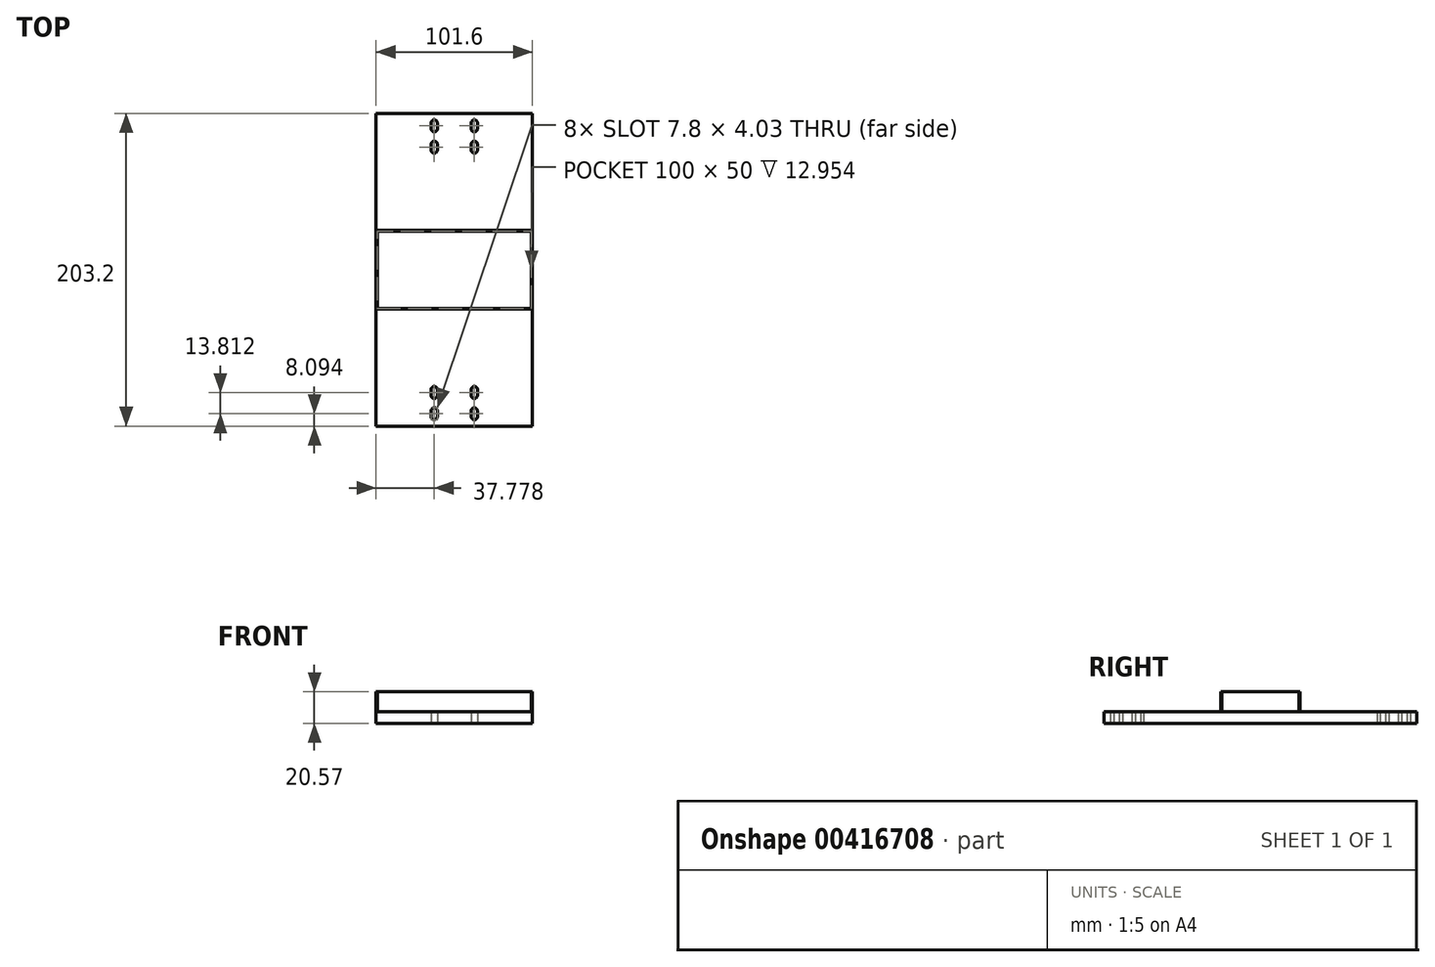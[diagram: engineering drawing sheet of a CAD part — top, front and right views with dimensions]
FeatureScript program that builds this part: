
annotation { "Feature Type Name" : "Feature", "Feature Type Description" : "" }
export const myFeature = defineFeature(function(context is Context, id is Id, definition is map)
    precondition{}
    {
        {
            var Q0;
            Q0=qCreatedBy(makeId("Top.planeOp"),FACE);
            var sketch = newSketch(context, id + "F0", { "sketchPlane" : qUnion([Q0])});
            skLineSegment(sketch, "E0.bottom", {"start": v(-50.8, 101.6) * mm, "end": v(50.8, 101.6) * mm});
            skLineSegment(sketch, "E0.top", {"start": v(-50.8, -101.6) * mm, "end": v(50.8, -101.6) * mm});
            skLineSegment(sketch, "E0.left", {"start": v(-50.8, 101.6) * mm, "end": v(-50.8, -101.6) * mm});
            skLineSegment(sketch, "E0.right", {"start": v(50.8, 101.6) * mm, "end": v(50.8, -101.6) * mm});
            skPoint(sketch, "E0.middle", {"position": v(0, 0) * mm});
            skSolve(sketch);
        }
        {
            var Q0;
            Q0=qSketchRegion(id+"F0",true);
            extrude(context, id + "F1", {"entities" : qUnion([Q0]), "depth" : 7.62 * mm});
        }
        {
            var Q0;
            Q0=qCreatedBy(makeId("Top.planeOp"),FACE);
            var sketch = newSketch(context, id + "F2", { "sketchPlane" : qUnion([Q0])});
            skLineSegment(sketch, "E1.top", {"start": v(-19, -101.6) * mm, "end": v(19, -101.6) * mm});
            skArc(sketch, "E2", {"start": v(-14.99, -81.42) * mm, "mid": v(-13.08, -83.6) * mm, "end": v(-11, -81.58) * mm});
            skArc(sketch, "E3", {"start": v(-11.05, -77.84) * mm, "mid": v(-13.03, -75.8) * mm, "end": v(-15.04, -77.82) * mm});
            skLineSegment(sketch, "E4", {"start": v(-11.05, -77.84) * mm, "end": v(-11, -81.58) * mm});
            skLineSegment(sketch, "E5", {"start": v(-15.04, -77.82) * mm, "end": v(-14.99, -81.42) * mm});
            skLineSegment(sketch, "E6.MirrorCS", {"start": v(-11.05, -95.36) * mm, "end": v(-11, -91.62) * mm});
            skLineSegment(sketch, "E7.MirrorCS", {"start": v(-15.04, -95.38) * mm, "end": v(-14.99, -91.78) * mm});
            skArc(sketch, "E8.MirrorCS", {"start": v(-14.99, -91.78) * mm, "mid": v(-13.08, -89.6) * mm, "end": v(-11, -91.62) * mm});
            skArc(sketch, "E9.MirrorCS", {"start": v(-11.05, -95.36) * mm, "mid": v(-13.03, -97.4) * mm, "end": v(-15.04, -95.38) * mm});
            skLineSegment(sketch, "E10.MirrorCS", {"start": v(11.05, -77.84) * mm, "end": v(11, -81.58) * mm});
            skLineSegment(sketch, "E11.MirrorCS", {"start": v(15.04, -77.82) * mm, "end": v(14.99, -81.42) * mm});
            skArc(sketch, "E12.MirrorCS", {"start": v(14.99, -81.42) * mm, "mid": v(13.08, -83.6) * mm, "end": v(11, -81.58) * mm});
            skArc(sketch, "E13.MirrorCS", {"start": v(11.05, -77.84) * mm, "mid": v(13.03, -75.8) * mm, "end": v(15.04, -77.82) * mm});
            skArc(sketch, "E14.MirrorCS", {"start": v(11.05, -95.36) * mm, "mid": v(13.03, -97.4) * mm, "end": v(15.04, -95.38) * mm});
            skLineSegment(sketch, "E15.MirrorCS", {"start": v(11.05, -95.36) * mm, "end": v(11, -91.62) * mm});
            skArc(sketch, "E16.MirrorCS", {"start": v(14.99, -91.78) * mm, "mid": v(13.08, -89.6) * mm, "end": v(11, -91.62) * mm});
            skLineSegment(sketch, "E17", {"start": v(14.99, -91.78) * mm, "end": v(15.04, -95.38) * mm});
            skLineSegment(sketch, "E18.MirrorCS", {"start": v(11.05, 95.36) * mm, "end": v(11, 91.62) * mm});
            skArc(sketch, "E19.MirrorCS", {"start": v(-11.05, 95.36) * mm, "mid": v(-13.03, 97.4) * mm, "end": v(-15.04, 95.38) * mm});
            skLineSegment(sketch, "E20.MirrorCS", {"start": v(-11.05, 77.84) * mm, "end": v(-11, 81.58) * mm});
            skLineSegment(sketch, "E21.MirrorCS", {"start": v(15.04, 77.82) * mm, "end": v(14.99, 81.42) * mm});
            skLineSegment(sketch, "E22.MirrorCS", {"start": v(11.05, 77.84) * mm, "end": v(11, 81.58) * mm});
            skArc(sketch, "E23.MirrorCS", {"start": v(11.05, 77.84) * mm, "mid": v(13.03, 75.8) * mm, "end": v(15.04, 77.82) * mm});
            skArc(sketch, "E24.MirrorCS", {"start": v(-14.99, 81.42) * mm, "mid": v(-13.08, 83.6) * mm, "end": v(-11, 81.58) * mm});
            skArc(sketch, "E25.MirrorCS", {"start": v(-11.05, 77.84) * mm, "mid": v(-13.03, 75.8) * mm, "end": v(-15.04, 77.82) * mm});
            skArc(sketch, "E26.MirrorCS", {"start": v(14.99, 91.78) * mm, "mid": v(13.08, 89.6) * mm, "end": v(11, 91.62) * mm});
            skLineSegment(sketch, "E27.MirrorCS", {"start": v(-15.04, 95.38) * mm, "end": v(-14.99, 91.78) * mm});
            skArc(sketch, "E28.MirrorCS", {"start": v(11.05, 95.36) * mm, "mid": v(13.03, 97.4) * mm, "end": v(15.04, 95.38) * mm});
            skLineSegment(sketch, "E29.MirrorCS", {"start": v(-15.04, 77.82) * mm, "end": v(-14.99, 81.42) * mm});
            skArc(sketch, "E30.MirrorCS", {"start": v(-14.99, 91.78) * mm, "mid": v(-13.08, 89.6) * mm, "end": v(-11, 91.62) * mm});
            skLineSegment(sketch, "E31.MirrorCS", {"start": v(14.99, 91.78) * mm, "end": v(15.04, 95.38) * mm});
            skLineSegment(sketch, "E32.MirrorCS", {"start": v(-11.05, 95.36) * mm, "end": v(-11, 91.62) * mm});
            skArc(sketch, "E33.MirrorCS", {"start": v(14.99, 81.42) * mm, "mid": v(13.08, 83.6) * mm, "end": v(11, 81.58) * mm});
            skSolve(sketch);
        }
        {
            var Q0;
            Q0=qSketchRegion(id+"F2",true);
            extrude(context, id + "F3", {"entities" : qUnion([Q0]), "operationType" : NewBodyOperationType.REMOVE, "oppositeDirection" : true, "depth" : -25.4 * mm});
        }
        {
            var Q0;
            Q0=makeQuery(id+"F1.opExtrude","CAP_FACE",FACE,{"disambiguationData":[OSD([sQuery(id+"F0.wireOp",EDGE,"E0.bottom"),sQuery(id+"F0.wireOp",EDGE,"E0.top"),sQuery(id+"F0.wireOp",EDGE,"E0.left"),sQuery(id+"F0.wireOp",EDGE,"E0.right")])],"isStart":false});
            var sketch = newSketch(context, id + "F4", { "sketchPlane" : qUnion([Q0])});
            skLineSegment(sketch, "E34.bottom", {"start": v(-50, 25) * mm, "end": v(50, 25) * mm});
            skLineSegment(sketch, "E34.top", {"start": v(-50, -25) * mm, "end": v(50, -25) * mm});
            skLineSegment(sketch, "E34.left", {"start": v(-50, 25) * mm, "end": v(-50, -25) * mm});
            skLineSegment(sketch, "E34.right", {"start": v(50, 25) * mm, "end": v(50, -25) * mm});
            skPoint(sketch, "E34.middle", {"position": v(0, 0) * mm});
            skLineSegment(sketch, "E35.0", {"start": v(-50, 25.58) * mm, "end": v(50, 25.58) * mm});
            skLineSegment(sketch, "E36.0", {"start": v(-50, -25.58) * mm, "end": v(50, -25.58) * mm});
            skLineSegment(sketch, "E37.0", {"start": v(50.76, 25) * mm, "end": v(50.76, -25) * mm});
            skLineSegment(sketch, "E38.0", {"start": v(-50.78, 25) * mm, "end": v(-50.78, -25) * mm});
            skLineSegment(sketch, "E39", {"start": v(50, 25.58) * mm, "end": v(50.76, 25) * mm});
            skLineSegment(sketch, "E40", {"start": v(-50.78, 25) * mm, "end": v(-50, 25.58) * mm});
            skLineSegment(sketch, "E41", {"start": v(-50.78, -25) * mm, "end": v(-50, -25.58) * mm});
            skLineSegment(sketch, "E42", {"start": v(50, -25.58) * mm, "end": v(50.76, -25) * mm});
            skSolve(sketch);
        }
        {
            var Q0;
            Q0=qSketchRegion(id+"F4",true);
            extrude(context, id + "F5", {"entities" : qUnion([Q0]), "operationType" : NewBodyOperationType.ADD, "depth" : 12.95 * mm});
        }
    });
